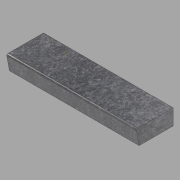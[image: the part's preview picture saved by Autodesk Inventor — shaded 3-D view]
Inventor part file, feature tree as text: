
AUTODESK INVENTOR PART (.ipt)
format: ipt  version: 2022.1 (Build 261234020, 234B)  size: 101,376 bytes
history: native  units: in
note: dims shown in document units (in); Inventor stores cm internally (conversion verified against a paired STEP export)
features: other x3, extrude x1, sketch x1
ambient origin geometry x8: Origin, YZ Plane, XZ Plane, XY Plane, X Axis, Y Axis, Z Axis, Center Point
bodies: Solid1 (feature_tree)
feature tree (5):
  other  "Blocks"
  extrude  "Extrusion1"  Depth=49.5in TaperAngle=0.0deg
  sketch  "Sketch1"  dims[d0=13.0in d1=6.0in d2=13.5in d3=0.5in d4=0.5in d5=49.5in d6=0.0in]
  other  "Profile"
  other  "Profile:1"
